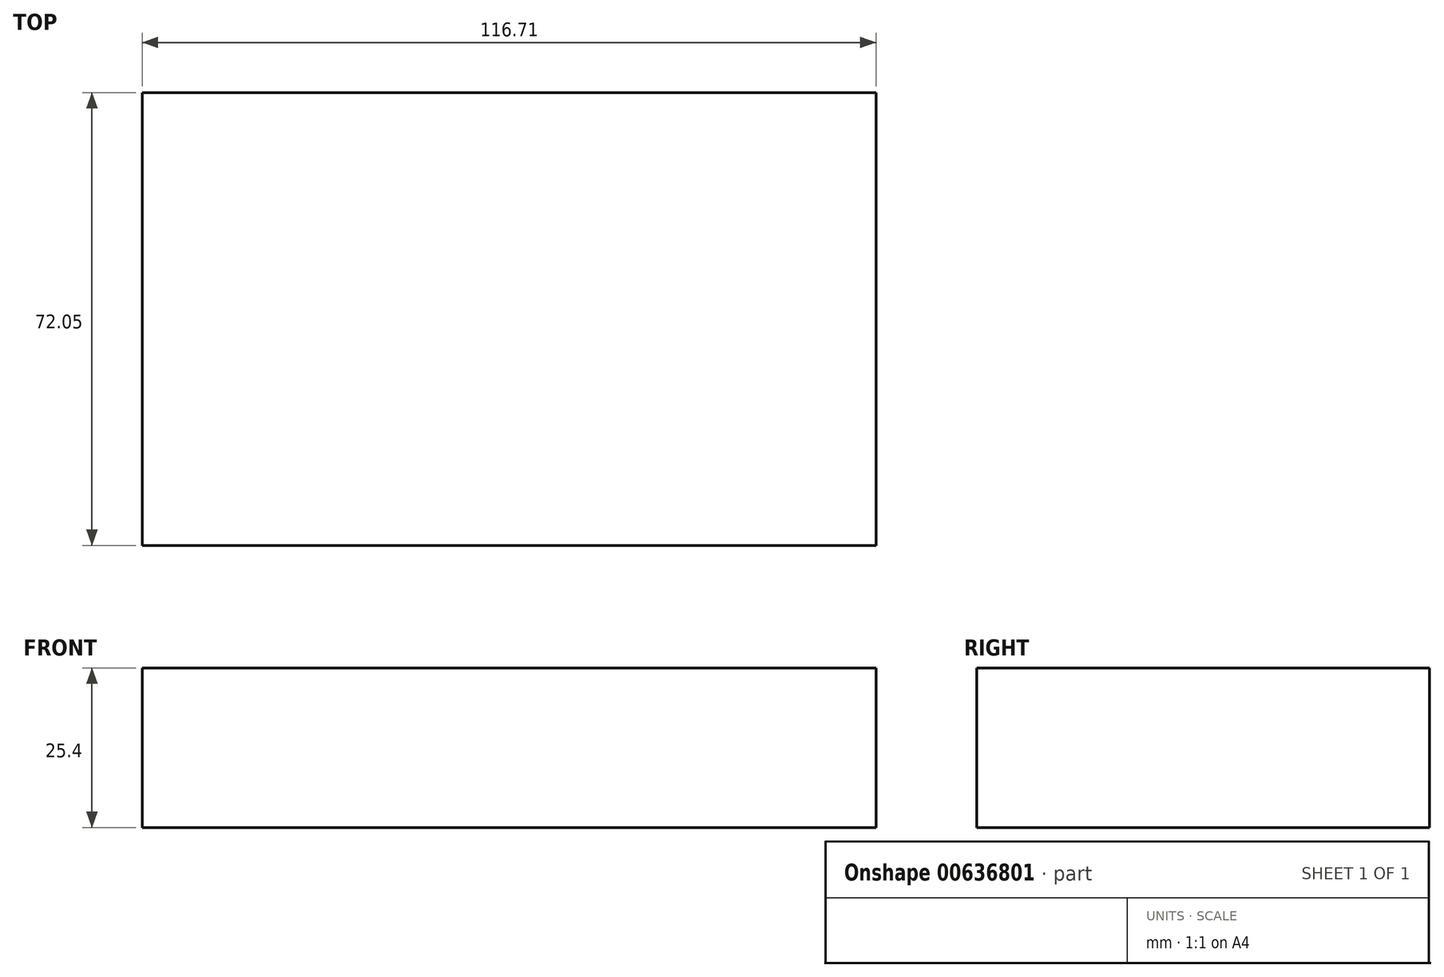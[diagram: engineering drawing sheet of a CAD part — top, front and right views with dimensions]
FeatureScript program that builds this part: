
annotation { "Feature Type Name" : "Feature", "Feature Type Description" : "" }
export const myFeature = defineFeature(function(context is Context, id is Id, definition is map)
    precondition{}
    {
        {
            var Q0;
            Q0=qCreatedBy(makeId("Top.planeOp"),FACE);
            var sketch = newSketch(context, id + "F0", { "sketchPlane" : qUnion([Q0])});
            skLineSegment(sketch, "E0.bottom", {"start": v(-63.06, 35.03) * mm, "end": v(53.65, 35.03) * mm});
            skLineSegment(sketch, "E0.top", {"start": v(-63.06, -37.02) * mm, "end": v(53.65, -37.02) * mm});
            skLineSegment(sketch, "E0.left", {"start": v(-63.06, 35.03) * mm, "end": v(-63.06, -37.02) * mm});
            skLineSegment(sketch, "E0.right", {"start": v(53.65, 35.03) * mm, "end": v(53.65, -37.02) * mm});
            skSolve(sketch);
        }
        {
            var Q0;
            Q0=makeQuery(id+"F0.imprint","IMPRINT",FACE,{"disambiguationData":[TD([[makeQuery(id+"F0.imprint","IMPRINT",EDGE,{"derivedFrom":sQuery(id+"F0.wireOp",EDGE,"E0.bottom")}),-1.0]])]});
            var Q1;
            Q1 = qSketchRegion(id + "F0", true);
            extrude(context, id + "F1", {"entities" : qUnion([Q0, Q1]), "depth" : 25.4 * mm, "offsetDistance" : 25.4 * mm});
        }
    });
